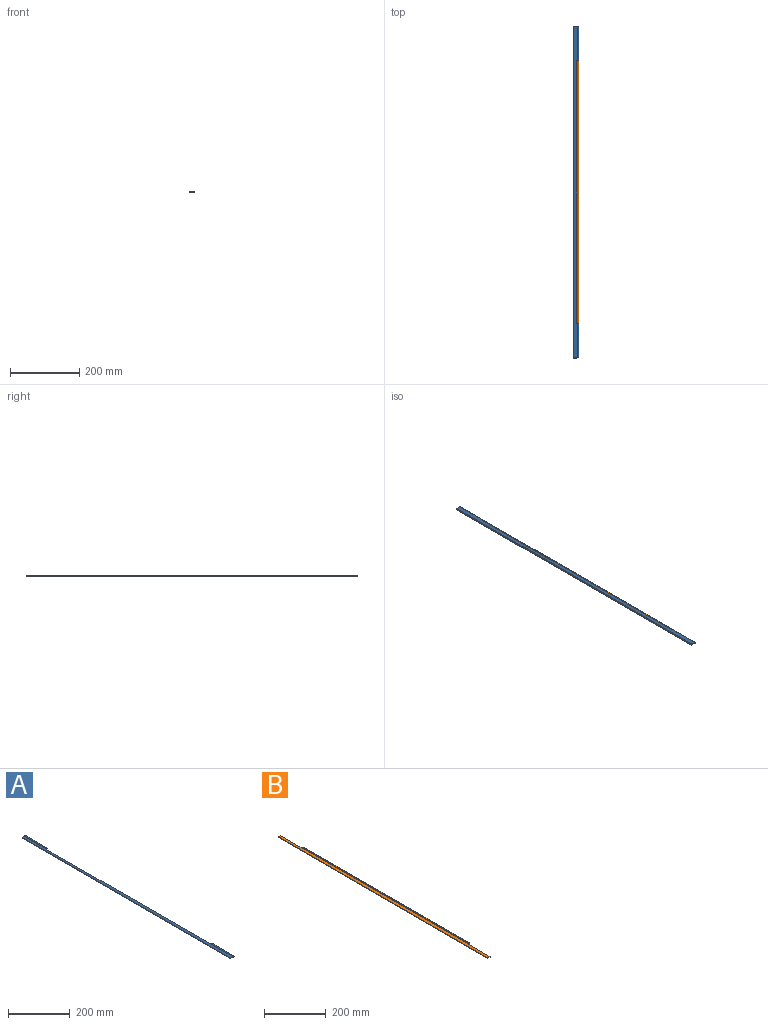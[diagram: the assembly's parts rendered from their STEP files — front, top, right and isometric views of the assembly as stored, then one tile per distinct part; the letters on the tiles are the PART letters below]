
ASSEMBLY  parts=2 mates=1
PART A: 14 faces, bbox 15x960x4.6 mm
  f0: plane 100x0.84mm, normal (1,0,0), area 84mm2, adj f1,f5,f9,f11
  f1: cylinder r=2mm len=100mm, axis (0,1,0), area 1106.1mm2, adj f0,f2,f9,f11
  f2: plane 960x11.08mm, normal (0,0,1), area 9816.1mm2, adj f1,f4,f7,f9,f10,f11,f12,f13
  f3: cylinder r=1mm len=100mm, axis (0,1,0), area 628.3mm2, adj f9,f11
  f4: plane 960x2mm, normal (-1,0,0), area 1920mm2, adj f2,f5,f9,f10
  f5: plane 960x11.98mm, normal (0,0,-1), area 9996.5mm2, adj f0,f4,f6,f9,f10,f11,f12,f13
  f6: plane 100x0.84mm, normal (1,0,0), area 84mm2, adj f5,f7,f10,f12
  f7: cylinder r=2mm len=100mm, axis (0,1,0), area 1106.1mm2, adj f2,f6,f10,f12
  f8: cylinder r=1mm len=100mm, axis (0,1,0), area 628.3mm2, adj f10,f12
  f9: plane 15x4.56mm, normal (0,-1,0), area 32.7mm2, adj f0,f1,f2,f3,f4,f5
  f10: plane 15x4.56mm, normal (0,1,0), area 32.7mm2, adj f2,f4,f5,f6,f7,f8
  f11: plane 5x4.56mm, normal (0,1,0), area 12.7mm2, adj f0,f1,f2,f3,f5,f13
  f12: plane 5x4.56mm, normal (0,-1,0), area 12.7mm2, adj f2,f5,f6,f7,f8,f13
  f13: plane 760x2mm, normal (1,0,0), area 1520mm2, adj f2,f5,f11,f12
PART B: 12 faces, bbox 15x960x4.6 mm
  f0: plane 960x11.98mm, normal (0,0,-1), area 11106.8mm2, adj f1,f4,f5,f6,f7,f8,f9,f10
  f1: plane 760x0.84mm, normal (1,0,0), area 638.1mm2, adj f0,f2,f7,f9
  f2: cylinder r=2mm len=760mm, axis (0,1,0), area 8406.5mm2, adj f1,f3,f7,f9
  f3: plane 960x11.08mm, normal (0,0,1), area 10421.1mm2, adj f2,f4,f5,f6,f7,f8,f9,f10
  f4: plane 960x2mm, normal (-1,0,0), area 1920mm2, adj f0,f3,f5,f6
  f5: plane 10x2mm, normal (0,-1,0), area 20mm2, adj f0,f3,f4,f10
  f6: plane 10x2mm, normal (0,1,0), area 20mm2, adj f0,f3,f4,f8
  f7: plane 5x4.56mm, normal (0,1,0), area 12.7mm2, adj f0,f1,f2,f3,f8,f11
  f8: plane 100x2mm, normal (1,0,0), area 200mm2, adj f0,f3,f6,f7
  f9: plane 5x4.56mm, normal (0,-1,0), area 12.7mm2, adj f0,f1,f2,f3,f10,f11
  f10: plane 100x2mm, normal (1,0,0), area 200mm2, adj f0,f3,f5,f9
  f11: cylinder r=1mm len=760mm, axis (0,1,0), area 4775.2mm2, adj f7,f9
PLACE A rot(axis=(-1,0,0),180deg) t=(-24.11,-799.84,16.09)mm
PLACE B t=(-24.11,160.16,10.97)mm
MATE revolute B.f2 <-> A.f1  axis (0,-1,0) through (-11.11,-699.84,13.53)mm
